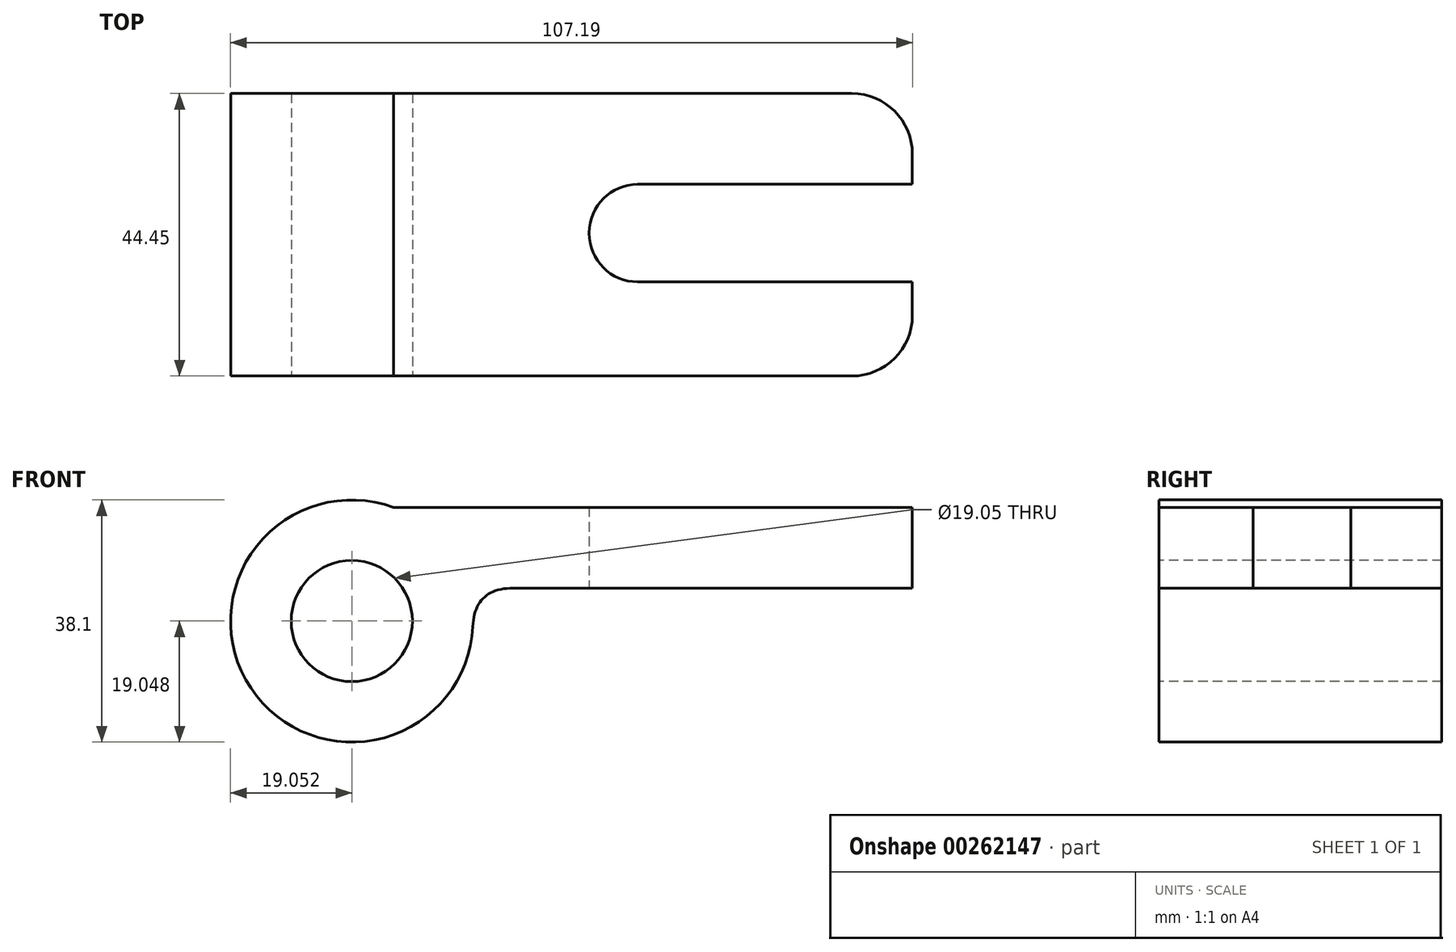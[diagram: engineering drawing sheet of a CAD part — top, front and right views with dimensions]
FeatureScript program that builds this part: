
annotation { "Feature Type Name" : "Feature", "Feature Type Description" : "" }
export const myFeature = defineFeature(function(context is Context, id is Id, definition is map)
    precondition{}
    {
        {
            var Q0;
            Q0=qCreatedBy(makeId("Front.planeOp"),FACE);
            var sketch = newSketch(context, id + "F0", { "sketchPlane" : qUnion([Q0])});
            skCircle(sketch, "E0", {"center": v(-59.29, 38.28) * mm, "radius": 19.05 * mm});
            skSolve(sketch);
        }
        {
            var Q0;
            Q0=makeQuery(id+"F0.imprint","IMPRINT",FACE,{"disambiguationData":[TD([[makeQuery(id+"F0.imprint","IMPRINT",EDGE,{"derivedFrom":sQuery(id+"F0.wireOp",EDGE,"E0")}),1.0]])]});
            extrude(context, id + "F1", {"entities" : qUnion([Q0]), "depth" : 44.45 * mm});
        }
        {
            var Q0;
            Q0=qCreatedBy(makeId("Front.planeOp"),FACE);
            var sketch = newSketch(context, id + "F2", { "sketchPlane" : qUnion([Q0])});
            skLineSegment(sketch, "E1.bottom", {"start": v(-60.05, 56.16) * mm, "end": v(28.85, 56.16) * mm});
            skLineSegment(sketch, "E1.top", {"start": v(-60.05, 43.46) * mm, "end": v(28.85, 43.46) * mm});
            skLineSegment(sketch, "E1.left", {"start": v(-60.05, 56.16) * mm, "end": v(-60.05, 43.46) * mm});
            skLineSegment(sketch, "E1.right", {"start": v(28.85, 56.16) * mm, "end": v(28.85, 43.46) * mm});
            skSolve(sketch);
        }
        {
            var Q0;
            Q0=makeQuery(id+"F2.imprint","IMPRINT",FACE,{"disambiguationData":[TD([[makeQuery(id+"F2.imprint","IMPRINT",EDGE,{"derivedFrom":sQuery(id+"F2.wireOp",EDGE,"E1.bottom")}),-1.0]])]});
            extrude(context, id + "F3", {"entities" : qUnion([Q0]), "operationType" : NewBodyOperationType.ADD, "depth" : 44.45 * mm});
        }
        {
            var Q0;
            Q0=makeQuery(id+"F3.boolean.opBoolean","INTERSECT",EDGE,{"derivedFrom":[makeQuery(id+"F1.opExtrude","SWEPT_FACE",FACE,{"disambiguationData":[OSD([sQuery(id+"F0.wireOp",EDGE,"E0")])]}),makeQuery(id+"F3.opExtrude","SWEPT_FACE",FACE,{"disambiguationData":[OSD([sQuery(id+"F2.wireOp",EDGE,"E1.top")])]})]});
            fillet(context, id + "F4", {"entities" : qUnion([Q0]), "radius" : 6.35 * mm, "rho" : 0.5, "crossSection" : FilletCrossSection.CONIC, "allowEdgeOverflow" : false});
        }
        {
            var Q0;
            Q0=makeQuery(id+"F3.boolean.opBoolean","MERGE",FACE,{"derivedFrom":[makeQuery(id+"F1.opExtrude","CAP_FACE",FACE,{"disambiguationData":[OSD([sQuery(id+"F0.wireOp",EDGE,"E0")])],"isStart":false}),makeQuery(id+"F3.opExtrude","CAP_FACE",FACE,{"disambiguationData":[OSD([sQuery(id+"F2.wireOp",EDGE,"E1.bottom"),sQuery(id+"F2.wireOp",EDGE,"E1.top"),sQuery(id+"F2.wireOp",EDGE,"E1.left"),sQuery(id+"F2.wireOp",EDGE,"E1.right")])],"isStart":false})]});
            var sketch = newSketch(context, id + "F5", { "sketchPlane" : qUnion([Q0])});
            skCircle(sketch, "E2", {"center": v(-59.29, 38.28) * mm, "radius": 9.53 * mm});
            skSolve(sketch);
        }
        {
            var Q0;
            Q0=makeQuery(id+"F5.imprint","IMPRINT",FACE,{"disambiguationData":[TD([[makeQuery(id+"F5.imprint","IMPRINT",EDGE,{"derivedFrom":sQuery(id+"F5.wireOp",EDGE,"E2")}),1.0]])]});
            extrude(context, id + "F6", {"entities" : qUnion([Q0]), "operationType" : NewBodyOperationType.REMOVE, "oppositeDirection" : true, "depth" : 44.45 * mm});
        }
        {
            var Q0;
            Q0=makeQuery(id+"F3.opExtrude","SWEPT_FACE",FACE,{"disambiguationData":[OSD([sQuery(id+"F2.wireOp",EDGE,"E1.top")])]});
            var sketch = newSketch(context, id + "F7", { "sketchPlane" : qUnion([Q0])});
            skLineSegment(sketch, "E3.bottom", {"start": v(28.85, 29.64) * mm, "end": v(-21.95, 29.64) * mm});
            skLineSegment(sketch, "E3.top", {"start": v(28.85, 14.29) * mm, "end": v(-21.95, 14.29) * mm});
            skLineSegment(sketch, "E3.left", {"start": v(28.85, 29.64) * mm, "end": v(28.85, 14.29) * mm});
            skLineSegment(sketch, "E3.right", {"start": v(-21.95, 29.64) * mm, "end": v(-21.95, 14.29) * mm});
            skSolve(sketch);
        }
        {
            var Q0;
            Q0=makeQuery(id+"F7.imprint","IMPRINT",FACE,{"disambiguationData":[TD([[makeQuery(id+"F7.imprint","IMPRINT",EDGE,{"derivedFrom":sQuery(id+"F7.wireOp",EDGE,"E3.bottom")}),1.0]])]});
            extrude(context, id + "F8", {"entities" : qUnion([Q0]), "operationType" : NewBodyOperationType.REMOVE, "oppositeDirection" : true, "depth" : 12.7 * mm});
        }
        {
            var Q0;
            Q0=makeQuery(id+"F8.boolean.opBoolean","COPY",EDGE,{"derivedFrom":makeQuery(id+"F8.opExtrude","SWEPT_EDGE",EDGE,{"disambiguationData":[OSD([sQuery(id+"F7.wireOp",EDGE,"E3.bottom"),sQuery(id+"F7.wireOp",EDGE,"E3.right")])]})});
            fillet(context, id + "F9", {"entities" : qUnion([Q0]), "radius" : 7.62 * mm, "tangentPropagation" : true, "allowEdgeOverflow" : false});
        }
        {
            var Q0;
            Q0=makeQuery(id+"F8.boolean.opBoolean","COPY",EDGE,{"derivedFrom":makeQuery(id+"F8.opExtrude","SWEPT_EDGE",EDGE,{"disambiguationData":[OSD([sQuery(id+"F7.wireOp",EDGE,"E3.top"),sQuery(id+"F7.wireOp",EDGE,"E3.right")])]})});
            fillet(context, id + "F10", {"entities" : qUnion([Q0]), "radius" : 7.62 * mm, "tangentPropagation" : true, "allowEdgeOverflow" : false});
        }
        {
            var Q0;
            Q0=makeQuery(id+"F3.opExtrude","CAP_EDGE",EDGE,{"disambiguationData":[OSD([sQuery(id+"F2.wireOp",EDGE,"E1.right")])],"isStart":true});
            fillet(context, id + "F11", {"entities" : qUnion([Q0]), "radius" : 9.52 * mm, "tangentPropagation" : true, "allowEdgeOverflow" : false});
        }
        {
            var Q0;
            Q0=makeQuery(id+"F3.opExtrude","CAP_EDGE",EDGE,{"disambiguationData":[OSD([sQuery(id+"F2.wireOp",EDGE,"E1.right")])],"isStart":false});
            fillet(context, id + "F12", {"entities" : qUnion([Q0]), "radius" : 9.52 * mm, "tangentPropagation" : true, "allowEdgeOverflow" : false});
        }
    });
